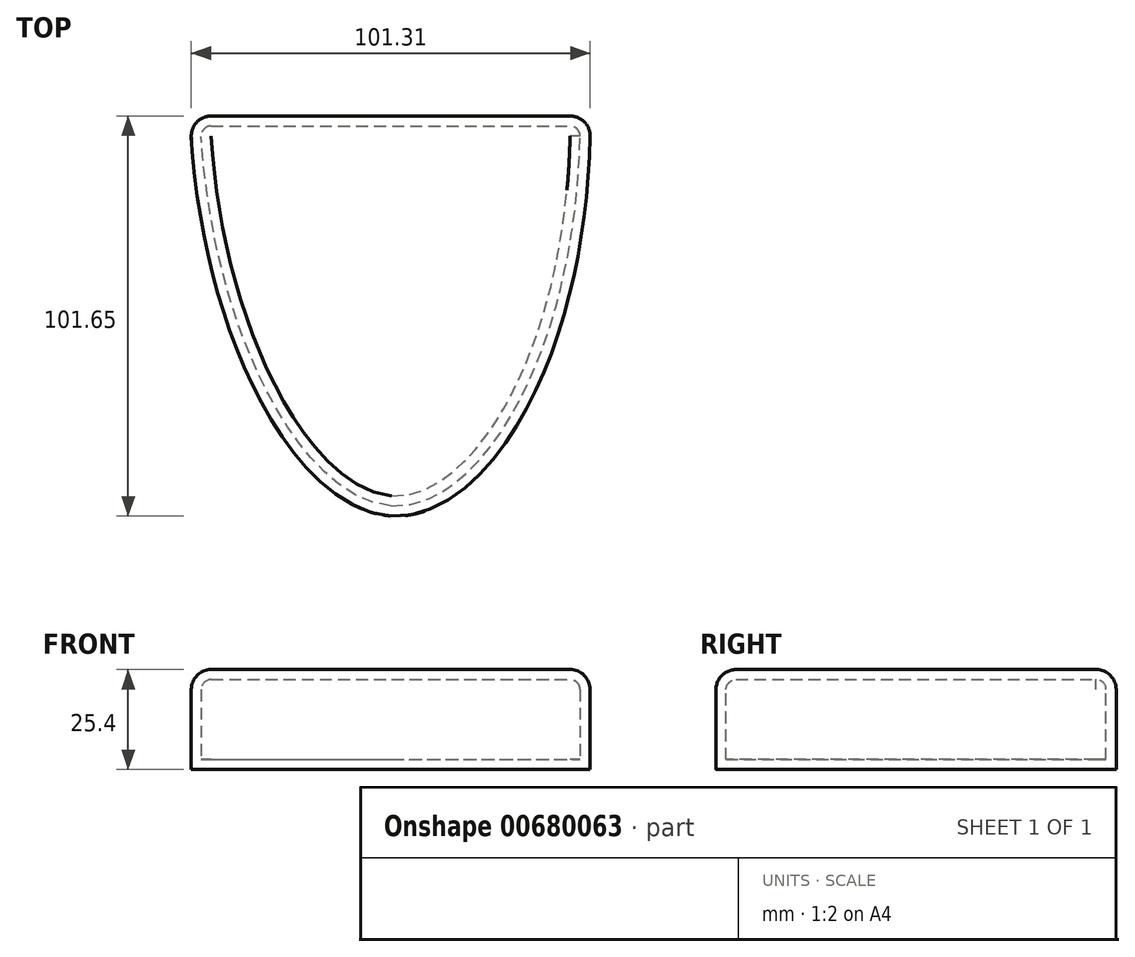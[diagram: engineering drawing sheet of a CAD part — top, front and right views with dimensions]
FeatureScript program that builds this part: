
annotation { "Feature Type Name" : "Feature", "Feature Type Description" : "" }
export const myFeature = defineFeature(function(context is Context, id is Id, definition is map)
    precondition{}
    {
        {
            var Q0;
            Q0=qCreatedBy(makeId("Top.planeOp"),FACE);
            var sketch = newSketch(context, id + "F0", { "sketchPlane" : qUnion([Q0])});
            skLineSegment(sketch, "E0", {"start": v(0, 48.4) * mm, "end": v(50.8, 48.4) * mm});
            skLineSegment(sketch, "E1", {"start": v(50.8, 48.4) * mm, "end": v(-50.8, 48.4) * mm});
            skLineSegment(sketch, "E2", {"start": v(0, 48.4) * mm, "end": v(0, -53.2) * mm});
            skFitSpline(sketch, "E3", {"points": [v(-50.8, 48.4) * mm, v(0, -53.2) * mm, v(50.8, 48.4) * mm], "startDerivative": vector(10.27, -318.7) * mm, "endDerivative": vector(-1.04, 359.81) * mm});
            skSolve(sketch);
        }
        {
            var Q0;
            Q0 = qSketchRegion(id + "F0", true);
            extrude(context, id + "F1", {"entities" : qUnion([Q0]), "depth" : 25.4 * mm, "offsetDistance" : 25.4 * mm});
        }
        {
            var Q0;
            Q0=makeQuery(id+"F1.opExtrude","CAP_EDGE",EDGE,{"disambiguationData":[OSD([sQuery(id+"F0.wireOp",EDGE,"E3")])],"isStart":false});
            fillet(context, id + "F2", {"entities" : qUnion([Q0]), "radius" : 5.08 * mm, "tangentPropagation" : true, "allowEdgeOverflow" : false});
        }
        {
            var Q0;
            Q0=makeQuery(id+"F1.opExtrude","CAP_EDGE",EDGE,{"disambiguationData":[OSD([sQuery(id+"F0.wireOp",EDGE,"E1")])],"isStart":false});
            fillet(context, id + "F3", {"entities" : qUnion([Q0]), "radius" : 5.08 * mm, "tangentPropagation" : true, "allowEdgeOverflow" : false});
        }
        {
            var Q0;
            Q0=makeQuery(id+"F1.opExtrude","CAP_FACE",FACE,{"disambiguationData":[OSD([sQuery(id+"F0.wireOp",EDGE,"E1"),sQuery(id+"F0.wireOp",EDGE,"E3")])],"isStart":false});
            var Q1;
            Q1=makeQuery(id+"F1.opExtrude","SWEPT_BODY",BODY,{"disambiguationData":[OSD([sQuery(id+"F0.wireOp",EDGE,"E1"),sQuery(id+"F0.wireOp",EDGE,"E3")])]});
            shell(context, id + "F4", {"isHollow" : true, "entities" : qUnion([Q0]), "parts" : qUnion([Q1]), "thickness" : 2.54 * mm});
        }
    });
